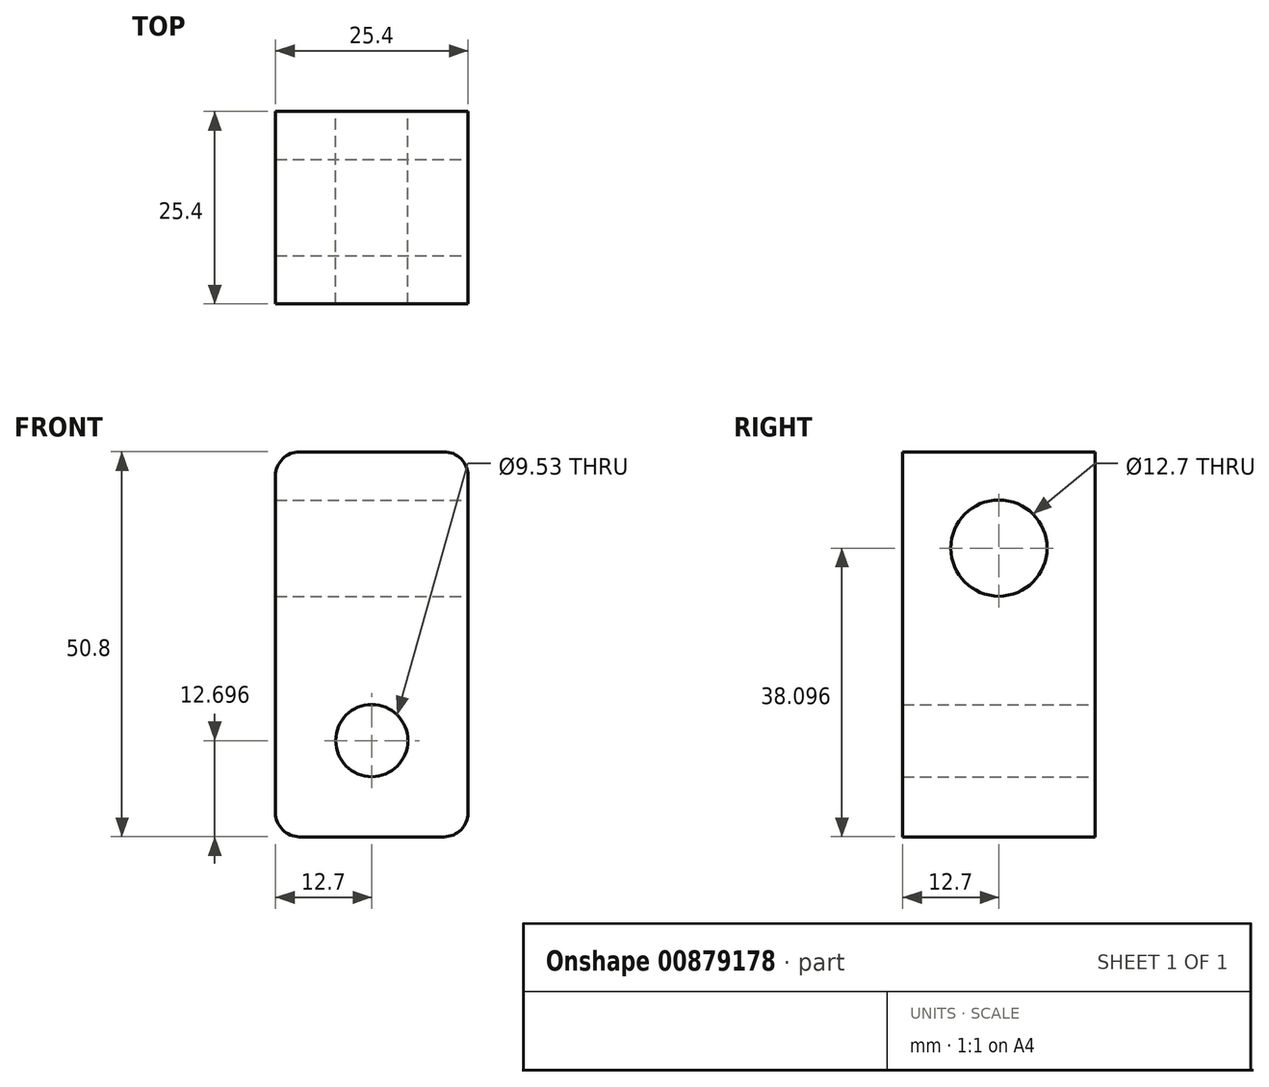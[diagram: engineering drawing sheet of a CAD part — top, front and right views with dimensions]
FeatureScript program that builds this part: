
annotation { "Feature Type Name" : "Feature", "Feature Type Description" : "" }
export const myFeature = defineFeature(function(context is Context, id is Id, definition is map)
    precondition{}
    {
        {
            var Q0;
            Q0=qCreatedBy(makeId("Front.planeOp"),FACE);
            var sketch = newSketch(context, id + "F0", { "sketchPlane" : qUnion([Q0])});
            skLineSegment(sketch, "E0.bottom", {"start": v(-17.58, -29.56) * mm, "end": v(1.47, -29.56) * mm});
            skLineSegment(sketch, "E0.top", {"start": v(-17.58, 21.24) * mm, "end": v(1.47, 21.24) * mm});
            skLineSegment(sketch, "E0.left", {"start": v(-20.75, -26.39) * mm, "end": v(-20.75, 18.06) * mm});
            skLineSegment(sketch, "E0.right", {"start": v(4.65, -26.39) * mm, "end": v(4.65, 18.06) * mm});
            skPoint(sketch, "E1.visualSharp", {"position": v(-20.75, 21.24) * mm});
            skArc(sketch, "E1.filletArc", {"start": v(-17.58, 21.24) * mm, "mid": v(-19.82, 20.3) * mm, "end": v(-20.75, 18.06) * mm});
            skPoint(sketch, "E2.visualSharp", {"position": v(4.65, 21.24) * mm});
            skArc(sketch, "E2.filletArc", {"start": v(4.65, 18.06) * mm, "mid": v(3.72, 20.3) * mm, "end": v(1.47, 21.24) * mm});
            skPoint(sketch, "E3.visualSharp", {"position": v(-20.75, -29.56) * mm});
            skArc(sketch, "E3.filletArc", {"start": v(-20.75, -26.39) * mm, "mid": v(-19.82, -28.63) * mm, "end": v(-17.58, -29.56) * mm});
            skPoint(sketch, "E4.visualSharp", {"position": v(4.65, -29.56) * mm});
            skArc(sketch, "E4.filletArc", {"start": v(1.47, -29.56) * mm, "mid": v(3.72, -28.63) * mm, "end": v(4.65, -26.39) * mm});
            skSolve(sketch);
        }
        {
            var Q0;
            Q0=qSketchRegion(id+"F0",true);
            extrude(context, id + "F1", {"entities" : qUnion([Q0]), "depth" : 25.4 * mm, "offsetDistance" : 25.4 * mm});
        }
        {
            var Q0;
            Q0=makeQuery(id+"F1.opExtrude","SWEPT_FACE",FACE,{"disambiguationData":[OSD([sQuery(id+"F0.wireOp",EDGE,"E0.right")])]});
            var sketch = newSketch(context, id + "F2", { "sketchPlane" : qUnion([Q0])});
            skCircle(sketch, "E5", {"center": v(-12.7, 8.54) * mm, "radius": 6.35 * mm});
            skSolve(sketch);
        }
        {
            var Q0;
            Q0=qSketchRegion(id+"F2",true);
            extrude(context, id + "F3", {"entities" : qUnion([Q0]), "operationType" : NewBodyOperationType.REMOVE, "oppositeDirection" : true, "depth" : 25.4 * mm, "offsetDistance" : 25.4 * mm});
        }
        {
            var Q0;
            Q0=makeQuery(id+"F1.opExtrude","CAP_FACE",FACE,{"disambiguationData":[OSD([sQuery(id+"F0.wireOp",EDGE,"E0.bottom"),sQuery(id+"F0.wireOp",EDGE,"E0.top"),sQuery(id+"F0.wireOp",EDGE,"E0.left"),sQuery(id+"F0.wireOp",EDGE,"E0.right"),sQuery(id+"F0.wireOp",EDGE,"E1.filletArc"),sQuery(id+"F0.wireOp",EDGE,"E2.filletArc"),sQuery(id+"F0.wireOp",EDGE,"E3.filletArc"),sQuery(id+"F0.wireOp",EDGE,"E4.filletArc")])],"isStart":true});
            var sketch = newSketch(context, id + "F4", { "sketchPlane" : qUnion([Q0])});
            skCircle(sketch, "E6", {"center": v(8.05, -16.86) * mm, "radius": 4.76 * mm});
            skSolve(sketch);
        }
        {
            var Q0;
            Q0=qSketchRegion(id+"F4",true);
            extrude(context, id + "F5", {"entities" : qUnion([Q0]), "operationType" : NewBodyOperationType.REMOVE, "oppositeDirection" : true, "depth" : 25.4 * mm, "offsetDistance" : 25.4 * mm});
        }
    });
